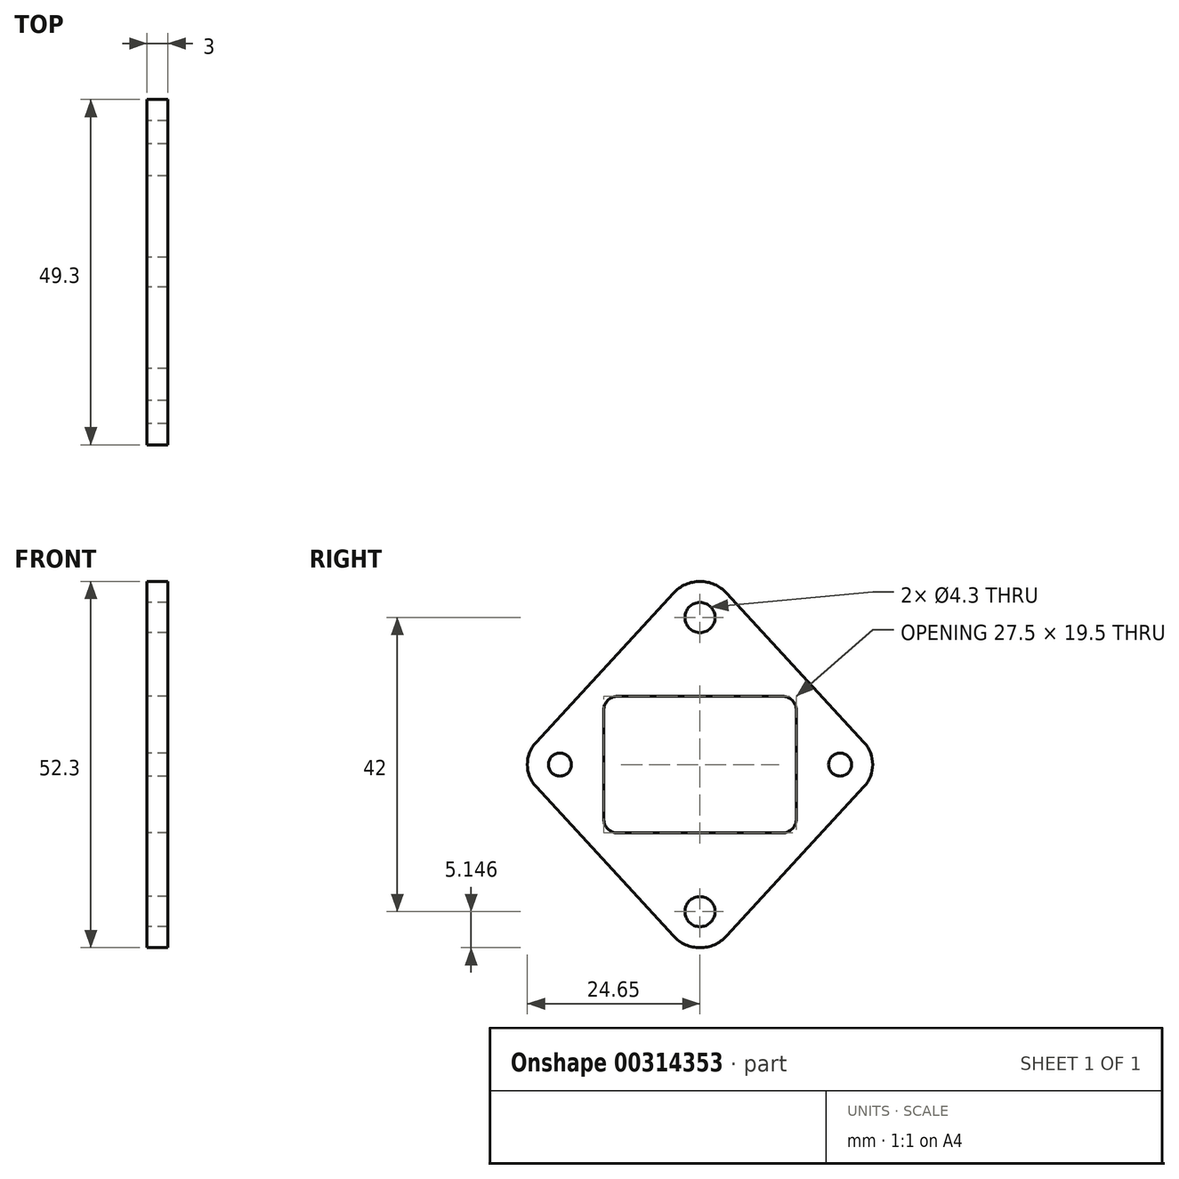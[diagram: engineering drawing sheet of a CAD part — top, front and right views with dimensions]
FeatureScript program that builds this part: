
annotation { "Feature Type Name" : "Feature", "Feature Type Description" : "" }
export const myFeature = defineFeature(function(context is Context, id is Id, definition is map)
    precondition{}
    {
        {
            var Q0;
            Q0=qCreatedBy(makeId("Right.planeOp"),FACE);
            var sketch = newSketch(context, id + "F0", { "sketchPlane" : qUnion([Q0])});
            skCircle(sketch, "E0", {"center": v(0, 37.52) * mm, "radius": 2.15 * mm});
            skCircle(sketch, "E1", {"center": v(0, -4.48) * mm, "radius": 2.15 * mm});
            skLineSegment(sketch, "E2", {"start": v(0, 37.52) * mm, "end": v(0, -4.48) * mm, "construction": true});
            skLineSegment(sketch, "E3.bottom", {"start": v(-11.75, 26.27) * mm, "end": v(11.75, 26.27) * mm});
            skLineSegment(sketch, "E3.top", {"start": v(-11.75, 6.77) * mm, "end": v(11.75, 6.77) * mm});
            skLineSegment(sketch, "E3.left", {"start": v(-13.75, 24.27) * mm, "end": v(-13.75, 8.77) * mm});
            skLineSegment(sketch, "E3.right", {"start": v(13.75, 24.27) * mm, "end": v(13.75, 8.77) * mm});
            skPoint(sketch, "E3.middle", {"position": v(0, 16.52) * mm});
            skArc(sketch, "E4.0", {"start": v(3.79, 41) * mm, "mid": v(0, 42.67) * mm, "end": v(-3.79, 41) * mm});
            skArc(sketch, "E5.0", {"start": v(-3.79, -7.97) * mm, "mid": v(0, -9.63) * mm, "end": v(3.79, -7.97) * mm});
            skCircle(sketch, "E6", {"center": v(-20, 16.52) * mm, "radius": 1.65 * mm});
            skCircle(sketch, "E7", {"center": v(20, 16.52) * mm, "radius": 1.65 * mm});
            skLineSegment(sketch, "E8", {"start": v(-20, 16.52) * mm, "end": v(20, 16.52) * mm, "construction": true});
            skArc(sketch, "E9.0", {"start": v(23.42, 13.37) * mm, "mid": v(24.65, 16.52) * mm, "end": v(23.42, 19.66) * mm});
            skLineSegment(sketch, "E10", {"start": v(-23.42, 19.66) * mm, "end": v(-3.79, 41) * mm});
            skLineSegment(sketch, "E11", {"start": v(-23.42, 13.37) * mm, "end": v(-3.79, -7.97) * mm});
            skLineSegment(sketch, "E12", {"start": v(3.79, 41) * mm, "end": v(23.42, 19.66) * mm});
            skLineSegment(sketch, "E13", {"start": v(23.42, 13.37) * mm, "end": v(3.79, -7.97) * mm});
            skArc(sketch, "E14.trimOffspring", {"start": v(-23.42, 19.66) * mm, "mid": v(-24.65, 16.52) * mm, "end": v(-23.42, 13.37) * mm});
            skPoint(sketch, "E15.visualSharp", {"position": v(-13.75, 6.77) * mm});
            skArc(sketch, "E15.filletArc", {"start": v(-13.75, 8.77) * mm, "mid": v(-13.16, 7.35) * mm, "end": v(-11.75, 6.77) * mm});
            skPoint(sketch, "E16.visualSharp", {"position": v(13.75, 6.77) * mm});
            skArc(sketch, "E16.filletArc", {"start": v(11.75, 6.77) * mm, "mid": v(13.16, 7.35) * mm, "end": v(13.75, 8.77) * mm});
            skPoint(sketch, "E17.visualSharp", {"position": v(13.75, 26.27) * mm});
            skArc(sketch, "E17.filletArc", {"start": v(13.75, 24.27) * mm, "mid": v(13.16, 25.68) * mm, "end": v(11.75, 26.27) * mm});
            skPoint(sketch, "E18.visualSharp", {"position": v(-13.75, 26.27) * mm});
            skArc(sketch, "E18.filletArc", {"start": v(-11.75, 26.27) * mm, "mid": v(-13.16, 25.68) * mm, "end": v(-13.75, 24.27) * mm});
            skSolve(sketch);
        }
        {
            var Q0;
            Q0 = qSketchRegion(id + "F0", true);
            extrude(context, id + "F1", {"entities" : qUnion([Q0]), "depth" : 3 * mm});
        }
    });
